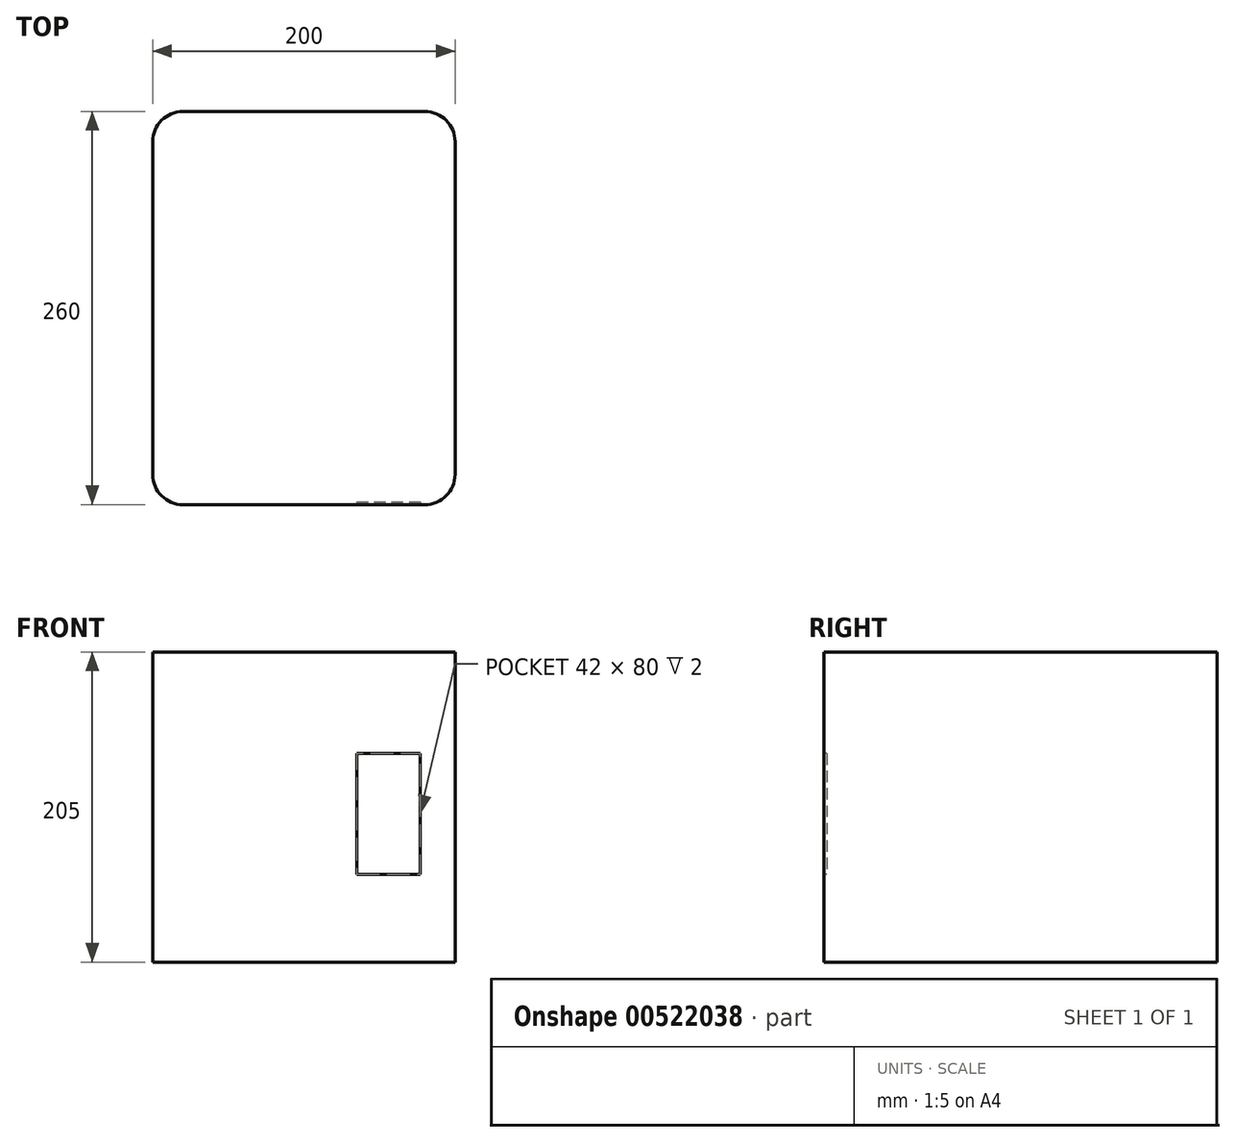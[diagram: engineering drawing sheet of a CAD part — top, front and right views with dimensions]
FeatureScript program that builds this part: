
annotation { "Feature Type Name" : "Feature", "Feature Type Description" : "" }
export const myFeature = defineFeature(function(context is Context, id is Id, definition is map)
    precondition{}
    {
        {
            var Q0;
            Q0=qCreatedBy(makeId("Top.planeOp"),FACE);
            var sketch = newSketch(context, id + "F0", { "sketchPlane" : qUnion([Q0])});
            skLineSegment(sketch, "E0.bottom", {"start": v(0, 0) * mm, "end": v(200, 0) * mm});
            skLineSegment(sketch, "E0.top", {"start": v(0, 260) * mm, "end": v(200, 260) * mm});
            skLineSegment(sketch, "E0.left", {"start": v(0, 0) * mm, "end": v(0, 260) * mm});
            skLineSegment(sketch, "E0.right", {"start": v(200, 0) * mm, "end": v(200, 260) * mm});
            skSolve(sketch);
        }
        {
            var Q0;
            Q0=makeQuery(id+"F0.imprint","IMPRINT",FACE,{"disambiguationData":[TD([[makeQuery(id+"F0.imprint","IMPRINT",EDGE,{"derivedFrom":sQuery(id+"F0.wireOp",EDGE,"E0.bottom")}),1.0]])]});
            extrude(context, id + "F1", {"entities" : qUnion([Q0]), "depth" : 205 * mm, "offsetDistance" : 25 * mm});
        }
        {
            var Q0;
            Q0=makeQuery(id+"F1.opExtrude","SWEPT_EDGE",EDGE,{"disambiguationData":[OSD([sQuery(id+"F0.wireOp",EDGE,"E0.bottom"),sQuery(id+"F0.wireOp",EDGE,"E0.left")])]});
            var Q1;
            Q1=makeQuery(id+"F1.opExtrude","SWEPT_EDGE",EDGE,{"disambiguationData":[OSD([sQuery(id+"F0.wireOp",EDGE,"E0.top"),sQuery(id+"F0.wireOp",EDGE,"E0.left")])]});
            var Q2;
            Q2=makeQuery(id+"F1.opExtrude","SWEPT_EDGE",EDGE,{"disambiguationData":[OSD([sQuery(id+"F0.wireOp",EDGE,"E0.top"),sQuery(id+"F0.wireOp",EDGE,"E0.right")])]});
            var Q3;
            Q3=makeQuery(id+"F1.opExtrude","SWEPT_EDGE",EDGE,{"disambiguationData":[OSD([sQuery(id+"F0.wireOp",EDGE,"E0.bottom"),sQuery(id+"F0.wireOp",EDGE,"E0.right")])]});
            fillet(context, id + "F2", {"entities" : qUnion([Q0, Q1, Q2, Q3]), "radius" : 20 * mm, "tangentPropagation" : true, "allowEdgeOverflow" : false});
        }
        {
            var Q0;
            Q0=makeQuery(id+"F1.opExtrude","SWEPT_FACE",FACE,{"disambiguationData":[OSD([sQuery(id+"F0.wireOp",EDGE,"E0.bottom")])]});
            var sketch = newSketch(context, id + "F3", { "sketchPlane" : qUnion([Q0])});
            skLineSegment(sketch, "E1.bottom", {"start": v(135, 138) * mm, "end": v(177, 138) * mm});
            skLineSegment(sketch, "E1.top", {"start": v(135, 58) * mm, "end": v(177, 58) * mm});
            skLineSegment(sketch, "E1.left", {"start": v(135, 138) * mm, "end": v(135, 58) * mm});
            skLineSegment(sketch, "E1.right", {"start": v(177, 138) * mm, "end": v(177, 58) * mm});
            skSolve(sketch);
        }
        {
            var Q0;
            Q0=makeQuery(id+"F3.imprint","IMPRINT",FACE,{"disambiguationData":[TD([[makeQuery(id+"F3.imprint","IMPRINT",EDGE,{"derivedFrom":sQuery(id+"F3.wireOp",EDGE,"E1.bottom")}),-1.0]])]});
            extrude(context, id + "F4", {"entities" : qUnion([Q0]), "operationType" : NewBodyOperationType.REMOVE, "oppositeDirection" : true, "depth" : 2 * mm, "offsetDistance" : 25 * mm});
        }
    });
